# Revit family: Deca_Torneira de teto_Tube_1198.TUB.TET
name_source: partatom
category: Plumbing Fixtures
units: mm (PartAtom-declared; Revit-internal decimal feet)

## family parameters
Cut with Voids When Loaded = No
Host = Face
Part Type = Normal
Room Calculation Point = No
Round Connector Dimension = Use Radius
Shared = No

## types (5) — shared parameters
Aprovado por = quattroD
Atendimento ao Cliente = 0800-0117073
Categoria = METAIS PARA BANHEIRO
Composição Anel Vedação = -
Composição Assento = -
Composição Básica = Liga de Cobre (bronze e latão),Plásticos de Engenharia,Elastômeros
Composição Componente = -
Consumo = -
Cor Interna = -
Cor Secundária = -
Cores Componente = -
Criado por = quattroD
Código Pai = 1198.TUB.TET
Description = Torneira de teto
Diâmetro Água Fria = 15 mm  [stored 0.0492126 ft]
Informações Complementares = -
Itens de Instalação = -
Linha = Tube
Manufacturer = Deca
Norma = NBR10281
Peso Líquido (Kg) = 4.342
Pressão máx. funcionamento = 40 MCA
Pressão mín. Aquec. Acúmulo = -
Pressão mín. Aquec. Passagem = -
Pressão mín. funcionamento = 2 MCA
Raio Água Fria = 8 mm  [stored 0.0262467 ft]
Saída de Esgoto = -
Segmento = Banheiro Luxo
Tipo de dispositivo economizador = Sim
Tipo de mecanismo utilizado = MVC -1/4 volta
Tipo de rosca de entrada = BSP NBR 8133
Tipo de rosca de saída = -
URL = www.deca.com.br
Vazão na Pressão máx. (L/min) = 8
Vazão na Pressão mín. (L/min) = 4
zero-valued in all types: CWFU, Default Elevation, HWFU, WFU

## per-type parameters (varying)
| type | Acompanha o Produto | Cor Principal | Material | Model |
| 1198.CT.TUB.TET.MT_Corten | Acompanha Aerador 8 L/Min | Corten | Deca_Corten | 1198.CT.TUB.TET.MT |
| 1198.C.TUB.TET_Cromado | Acompanha Aerador 8 L/Min | Cromado | Deca_Cromado | 1198.C.TUB.TET |
| 1198.GL.TUB.TET.MT_Gold Matte | Acompanha Aerador 8 L/Min | Gold Matte | Deca_Gold Matte | 1198.GL.TUB.TET.MT |
| 1198.GL.TUB.TET.RD_Red Gold | Acompanha Aerador 8 L/Min | Red Gold | Deca_Red Gold | 1198.GL.TUB.TET.RD |
| 1198.BL.TUB.TET.MT_Black Matte | - | Black Matte | Deca_Black Matte | 1198.BL.TUB.TET.MT |

note: source unit labels omitted for Vazão na Pressão máx. (L/min), Vazão na Pressão mín. (L/min) — the stored unit's dimension contradicts the parameter name (converter mislabeling)

note: [stored X ft] marks values corroborated as IEEE doubles in the binary element streams (Revit-internal decimal feet)

## geometry (parser evidence)
native form markers: Sweep x1
no freeform markers — native parametric forms only
